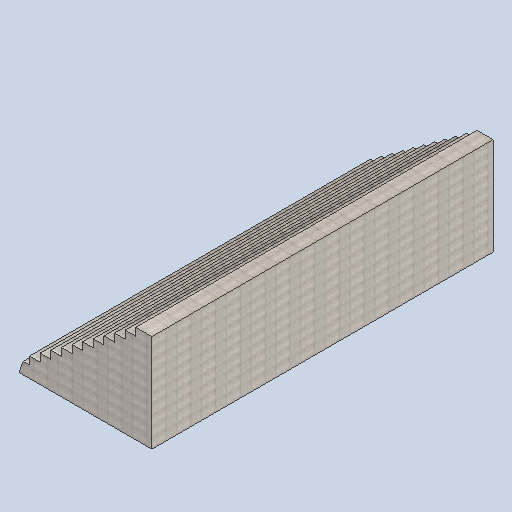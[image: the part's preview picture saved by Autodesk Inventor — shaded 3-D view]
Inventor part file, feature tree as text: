
AUTODESK INVENTOR PART (.ipt)
format: ipt  version: 2024.2 (Build 282272000, 272)  size: 238,080 bytes
history: native  units: in
note: dims shown in document units (in); Inventor stores cm internally (conversion verified against a paired STEP export)
features: other x3, sketch x3
ambient origin geometry x8: Origin, YZ Plane, XZ Plane, XY Plane, X Axis, Y Axis, Z Axis, Center Point
bodies: Solid1 (feature_tree)
feature tree (6):
  other  "front_stair.ipt"
  other  "Solid1::front_stair.ipt"
  other  "TaggingFeature1"
  sketch  "Sketch1"  dims[d0=0.3937in]
  sketch  "Sketch2"
  sketch  "Sketch3"
